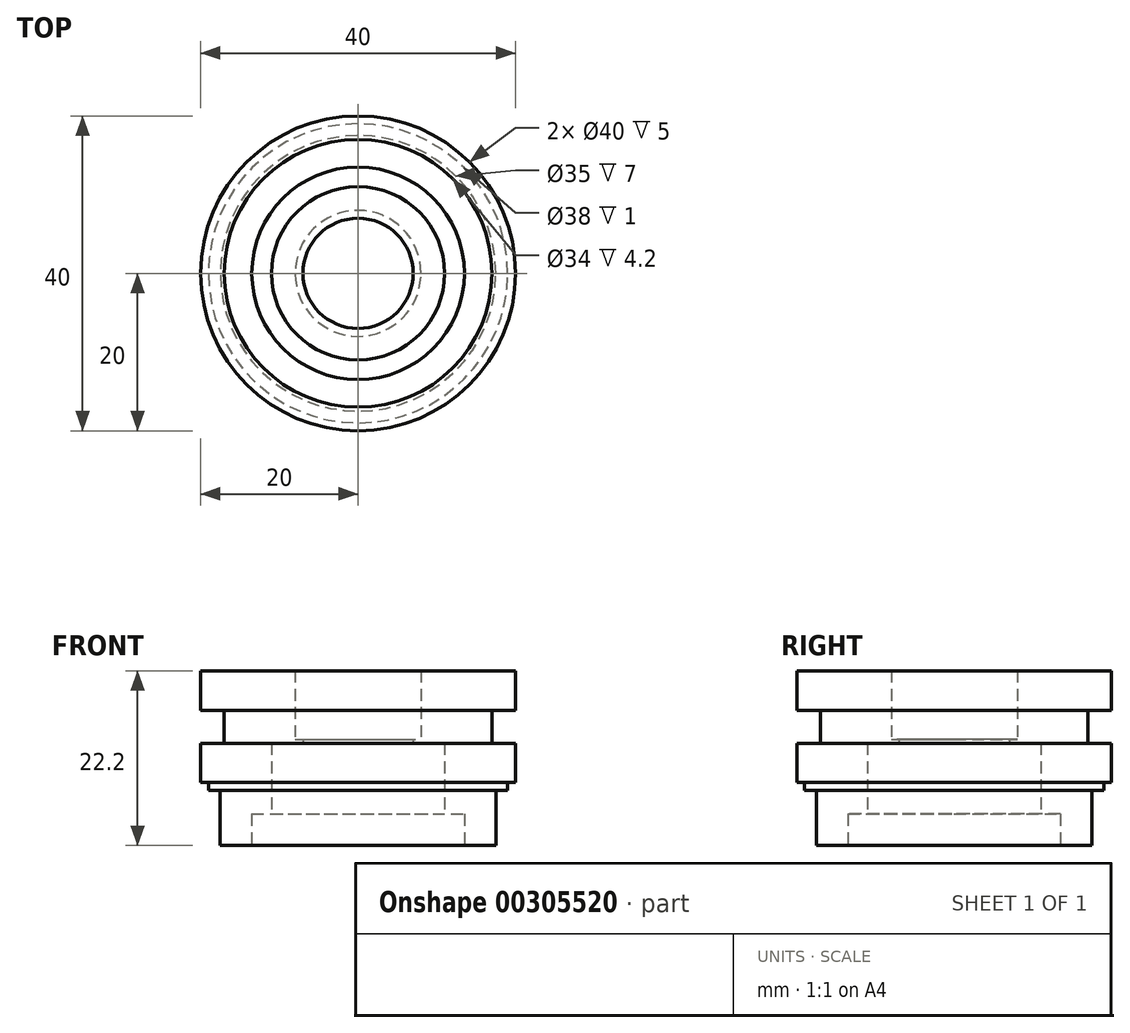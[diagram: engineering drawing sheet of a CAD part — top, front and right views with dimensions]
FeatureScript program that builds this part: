
annotation { "Feature Type Name" : "Feature", "Feature Type Description" : "" }
export const myFeature = defineFeature(function(context is Context, id is Id, definition is map)
    precondition{}
    {
        {
            var Q0;
            Q0=qCreatedBy(makeId("Front.planeOp"),FACE);
            var sketch = newSketch(context, id + "F0", { "sketchPlane" : qUnion([Q0])});
            skLineSegment(sketch, "E0", {"start": v(0, 0) * mm, "end": v(12, 0) * mm});
            skLineSegment(sketch, "E1", {"start": v(12, 0) * mm, "end": v(12, -5) * mm});
            skLineSegment(sketch, "E2", {"start": v(12, -5) * mm, "end": v(9, -5) * mm});
            skLineSegment(sketch, "E3", {"start": v(9, -5) * mm, "end": v(9, -9.2) * mm});
            skLineSegment(sketch, "E4", {"start": v(9, -9.2) * mm, "end": v(12, -9.2) * mm});
            skLineSegment(sketch, "E5", {"start": v(12, -9.2) * mm, "end": v(12, -14.2) * mm});
            skLineSegment(sketch, "E6", {"start": v(12, -14.2) * mm, "end": v(11, -14.2) * mm});
            skLineSegment(sketch, "E7", {"start": v(11, -14.2) * mm, "end": v(11, -15.2) * mm});
            skLineSegment(sketch, "E8", {"start": v(11, -15.2) * mm, "end": v(9.5, -15.2) * mm});
            skLineSegment(sketch, "E9", {"start": v(9.5, -15.2) * mm, "end": v(9.5, -22.2) * mm});
            skLineSegment(sketch, "E10", {"start": v(9.5, -22.2) * mm, "end": v(5.5, -22.2) * mm});
            skLineSegment(sketch, "E11", {"start": v(5.5, -22.2) * mm, "end": v(5.5, -18.2) * mm});
            skLineSegment(sketch, "E12", {"start": v(5.5, -18.2) * mm, "end": v(3, -18.2) * mm});
            skLineSegment(sketch, "E13", {"start": v(3, -18.2) * mm, "end": v(3, -9.2) * mm});
            skLineSegment(sketch, "E14", {"start": v(3, -9.2) * mm, "end": v(0, -9.2) * mm});
            skLineSegment(sketch, "E15", {"start": v(0, -8.7) * mm, "end": v(0, 0) * mm});
            skLineSegment(sketch, "E16", {"start": v(0, -9.2) * mm, "end": v(-1, -9.2) * mm});
            skLineSegment(sketch, "E17", {"start": v(-1, -9.2) * mm, "end": v(-1, -8.7) * mm});
            skLineSegment(sketch, "E18", {"start": v(-1, -8.7) * mm, "end": v(0, -8.7) * mm});
            skSolve(sketch);
        }
        {
            var Q0;
            Q0=qCreatedBy(makeId("Front.planeOp"),FACE);
            var sketch = newSketch(context, id + "F1", { "sketchPlane" : qUnion([Q0])});
            skLineSegment(sketch, "E19", {"start": v(-8, 6.5) * mm, "end": v(-8, -37.11) * mm, "construction": true});
            skSolve(sketch);
        }
        {
            var Q0;
            Q0 = qConstructionFilter(qBodyType(qCreatedBy(id + "F0" ,EDGE), BodyType.WIRE), ConstructionObject.NO);
            var Q1;
            Q1=sQuery(id+"F1.wireOp",EDGE,"E19");
            revolve(context, id + "F2", {"bodyType" : ToolBodyType.SURFACE, "surfaceEntities" : qUnion([Q0]), "axis" : qUnion([Q1]), "revolveType" : RevolveType.FULL});
        }
    });
